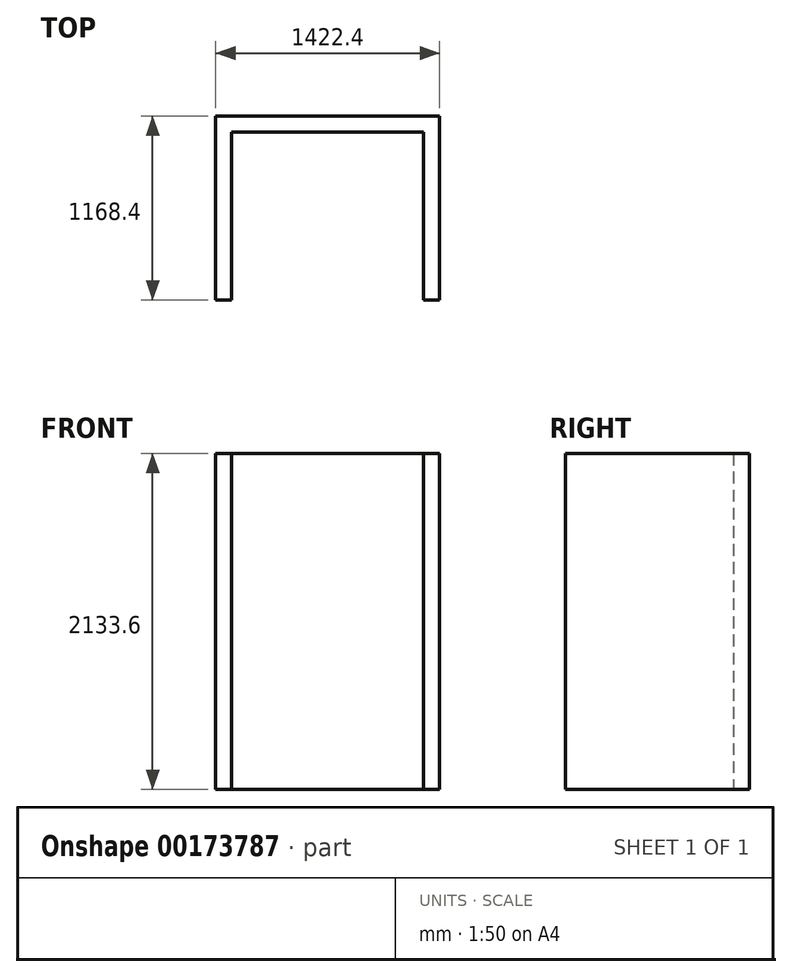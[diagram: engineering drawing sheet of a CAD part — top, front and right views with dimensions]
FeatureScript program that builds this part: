
annotation { "Feature Type Name" : "Feature", "Feature Type Description" : "" }
export const myFeature = defineFeature(function(context is Context, id is Id, definition is map)
    precondition{}
    {
        {
            var Q0;
            Q0=qCreatedBy(makeId("Top.planeOp"),FACE);
            var sketch = newSketch(context, id + "F0", { "sketchPlane" : qUnion([Q0])});
            skLineSegment(sketch, "E0.bottom", {"start": v(609.6, 533.4) * mm, "end": v(-609.6, 533.4) * mm});
            skLineSegment(sketch, "E0.left", {"start": v(609.6, 533.4) * mm, "end": v(609.6, -533.4) * mm});
            skLineSegment(sketch, "E0.right", {"start": v(-609.6, 533.4) * mm, "end": v(-609.6, -533.4) * mm});
            skPoint(sketch, "E0.middle", {"position": v(0, 0) * mm});
            skLineSegment(sketch, "E1", {"start": v(-609.6, -533.4) * mm, "end": v(-711.2, -533.4) * mm});
            skLineSegment(sketch, "E2", {"start": v(-711.2, -533.4) * mm, "end": v(-711.2, 635) * mm});
            skLineSegment(sketch, "E3", {"start": v(-711.2, 635) * mm, "end": v(711.2, 635) * mm});
            skLineSegment(sketch, "E4", {"start": v(711.2, 635) * mm, "end": v(711.2, -533.4) * mm});
            skLineSegment(sketch, "E5", {"start": v(711.2, -533.4) * mm, "end": v(609.6, -533.4) * mm});
            skLineSegment(sketch, "E6", {"start": v(-609.6, 533.4) * mm, "end": v(-711.2, 533.4) * mm, "construction": true});
            skLineSegment(sketch, "E7", {"start": v(609.6, 533.4) * mm, "end": v(711.2, 533.4) * mm, "construction": true});
            skLineSegment(sketch, "E8", {"start": v(609.6, 533.4) * mm, "end": v(609.6, 635) * mm, "construction": true});
            skLineSegment(sketch, "E9", {"start": v(-609.6, 533.4) * mm, "end": v(-609.6, 635) * mm, "construction": true});
            skSolve(sketch);
        }
        {
            var Q0;
            Q0=makeQuery(id+"F0.imprint","IMPRINT",FACE,{"disambiguationData":[TD([[makeQuery(id+"F0.imprint","IMPRINT",EDGE,{"derivedFrom":sQuery(id+"F0.wireOp",EDGE,"E0.bottom")}),-1.0]])]});
            extrude(context, id + "F1", {"entities" : qUnion([Q0]), "depth" : 2133.6 * mm});
        }
    });
